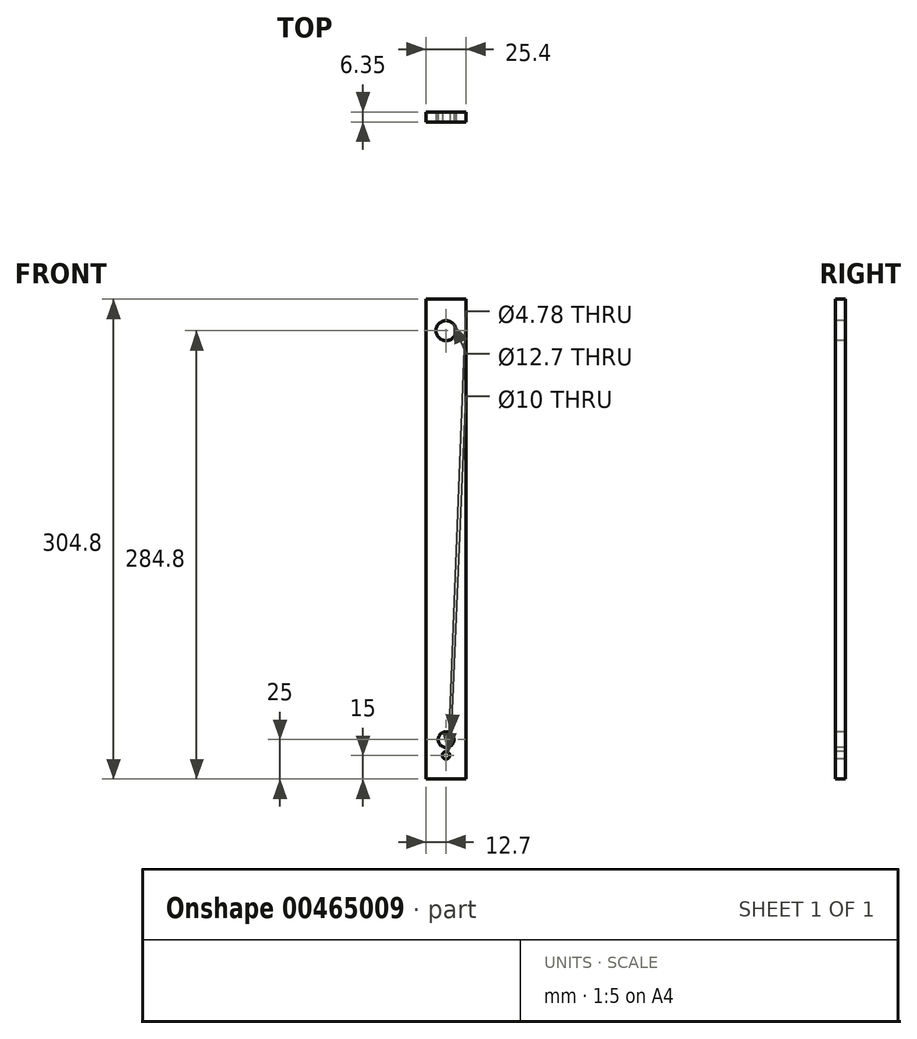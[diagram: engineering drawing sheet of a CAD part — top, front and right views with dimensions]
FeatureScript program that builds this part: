
annotation { "Feature Type Name" : "Feature", "Feature Type Description" : "" }
export const myFeature = defineFeature(function(context is Context, id is Id, definition is map)
    precondition{}
    {
        {
            var Q0;
            Q0=qCreatedBy(makeId("Front.planeOp"),FACE);
            var sketch = newSketch(context, id + "F0", { "sketchPlane" : qUnion([Q0])});
            skLineSegment(sketch, "E0.bottom", {"start": v(0, 0) * mm, "end": v(25.4, 0) * mm});
            skLineSegment(sketch, "E0.top", {"start": v(0, 304.8) * mm, "end": v(25.4, 304.8) * mm});
            skLineSegment(sketch, "E0.left", {"start": v(0, 0) * mm, "end": v(0, 304.8) * mm});
            skLineSegment(sketch, "E0.right", {"start": v(25.4, 0) * mm, "end": v(25.4, 304.8) * mm});
            skSolve(sketch);
        }
        {
            var Q0;
            Q0=makeQuery(id+"F0.imprint","IMPRINT",FACE,{"disambiguationData":[TD([[makeQuery(id+"F0.imprint","IMPRINT",EDGE,{"derivedFrom":sQuery(id+"F0.wireOp",EDGE,"E0.bottom")}),1.0]])]});
            extrude(context, id + "F1", {"entities" : qUnion([Q0]), "depth" : (0.25 * 25.4) * mm});
        }
        {
            var Q0;
            Q0=makeQuery(id+"F1.opExtrude","CAP_FACE",FACE,{"disambiguationData":[OSD([sQuery(id+"F0.wireOp",EDGE,"E0.bottom"),sQuery(id+"F0.wireOp",EDGE,"E0.top"),sQuery(id+"F0.wireOp",EDGE,"E0.left"),sQuery(id+"F0.wireOp",EDGE,"E0.right")])],"isStart":false});
            var sketch = newSketch(context, id + "F2", { "sketchPlane" : qUnion([Q0])});
            skLineSegment(sketch, "E1", {"start": v(12.7, 0) * mm, "end": v(12.7, 304.8) * mm, "construction": true});
            skCircle(sketch, "E2", {"center": v(12.7, 15) * mm, "radius": 2.39 * mm});
            skSolve(sketch);
        }
        {
            var Q0;
            Q0=makeQuery(id+"F2.imprint","IMPRINT",FACE,{"disambiguationData":[TD([[makeQuery(id+"F2.imprint","IMPRINT",EDGE,{"derivedFrom":sQuery(id+"F2.wireOp",EDGE,"E2")}),1.0]])]});
            extrude(context, id + "F3", {"entities" : qUnion([Q0]), "operationType" : NewBodyOperationType.REMOVE, "endBound" : BoundingType.THROUGH_ALL, "oppositeDirection" : true, "depth" : 25 * mm, "offsetDistance" : 25 * mm});
        }
        {
            var Q0;
            Q0=makeQuery(id+"F1.opExtrude","CAP_FACE",FACE,{"disambiguationData":[OSD([sQuery(id+"F0.wireOp",EDGE,"E0.bottom"),sQuery(id+"F0.wireOp",EDGE,"E0.top"),sQuery(id+"F0.wireOp",EDGE,"E0.left"),sQuery(id+"F0.wireOp",EDGE,"E0.right")])],"isStart":false});
            var sketch = newSketch(context, id + "F4", { "sketchPlane" : qUnion([Q0])});
            skLineSegment(sketch, "E3", {"start": v(12.7, 304.8) * mm, "end": v(12.7, 0) * mm, "construction": true});
            skCircle(sketch, "E4", {"center": v(12.7, 284.8) * mm, "radius": 6.35 * mm});
            skSolve(sketch);
        }
        {
            var Q0;
            Q0 = qSketchRegion(id + "F4", true);
            extrude(context, id + "F5", {"entities" : qUnion([Q0]), "operationType" : NewBodyOperationType.REMOVE, "endBound" : BoundingType.THROUGH_ALL, "oppositeDirection" : true, "depth" : 25 * mm});
        }
        {
            var Q0;
            Q0=makeQuery(id+"F1.opExtrude","CAP_FACE",FACE,{"disambiguationData":[OSD([sQuery(id+"F0.wireOp",EDGE,"E0.bottom"),sQuery(id+"F0.wireOp",EDGE,"E0.top"),sQuery(id+"F0.wireOp",EDGE,"E0.left"),sQuery(id+"F0.wireOp",EDGE,"E0.right")])],"isStart":false});
            var sketch = newSketch(context, id + "F6", { "sketchPlane" : qUnion([Q0])});
            skLineSegment(sketch, "E5", {"start": v(12.7, 15) * mm, "end": v(12.7, 76.16) * mm, "construction": true});
            skCircle(sketch, "E6", {"center": v(12.7, 25) * mm, "radius": 5 * mm});
            skSolve(sketch);
        }
        {
            var Q0;
            Q0 = qSketchRegion(id + "F6", true);
            extrude(context, id + "F7", {"entities" : qUnion([Q0]), "operationType" : NewBodyOperationType.REMOVE, "endBound" : BoundingType.THROUGH_ALL, "oppositeDirection" : true, "depth" : 25 * mm, "offsetDistance" : 25 * mm});
        }
    });
